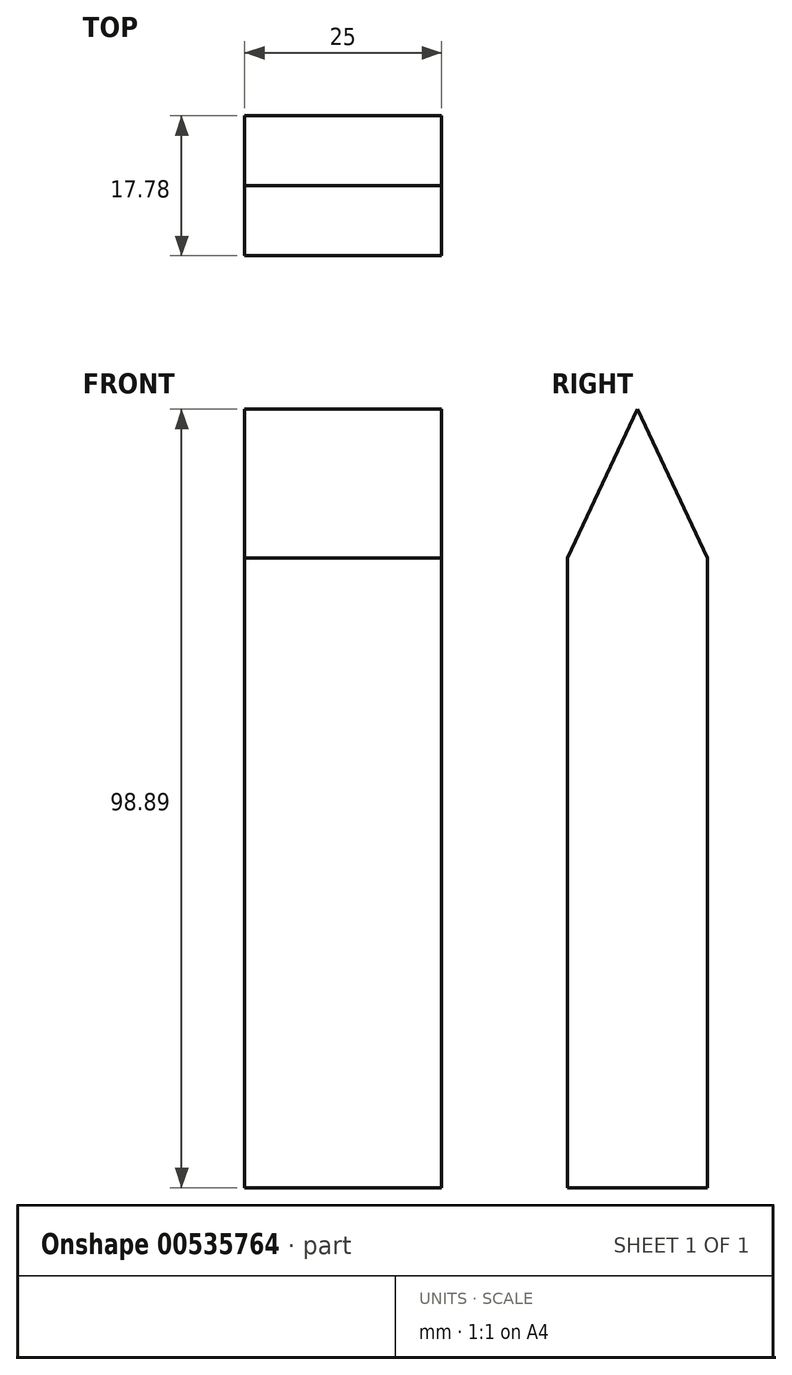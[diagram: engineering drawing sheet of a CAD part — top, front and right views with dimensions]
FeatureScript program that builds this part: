
annotation { "Feature Type Name" : "Feature", "Feature Type Description" : "" }
export const myFeature = defineFeature(function(context is Context, id is Id, definition is map)
    precondition{}
    {
        {
            var Q0;
            Q0=qCreatedBy(makeId("Right.planeOp"),FACE);
            var sketch = newSketch(context, id + "F0", { "sketchPlane" : qUnion([Q0])});
            skLineSegment(sketch, "E0", {"start": v(-35.56, 55.28) * mm, "end": v(-35.56, -24.72) * mm});
            skLineSegment(sketch, "E1", {"start": v(-35.56, -24.72) * mm, "end": v(-17.78, -24.72) * mm});
            skLineSegment(sketch, "E2", {"start": v(-17.78, -24.72) * mm, "end": v(-17.78, 55.28) * mm});
            skLineSegment(sketch, "E3", {"start": v(-17.78, 55.28) * mm, "end": v(-26.67, 74.17) * mm});
            skLineSegment(sketch, "E4", {"start": v(-26.67, 74.17) * mm, "end": v(-35.56, 55.28) * mm});
            skLineSegment(sketch, "E5", {"start": v(-62.22, 0) * mm, "end": v(-62.22, -22.5) * mm});
            skLineSegment(sketch, "E6", {"start": v(-62.22, 0) * mm, "end": v(-35.56, 15.28) * mm});
            skLineSegment(sketch, "E7", {"start": v(-62.22, -22.5) * mm, "end": v(-35.56, -8.06) * mm});
            skSolve(sketch);
        }
        {
            var Q0;
            {var subQ0=sQuery(id+"F0.wireOp",EDGE,"E1");Q0=makeQuery(id+"F0.imprint","IMPRINT",FACE,{"disambiguationData":[TD([[makeQuery(id+"F0.imprint","IMPRINT",EDGE,{"derivedFrom":subQ0}),1.0]])]});}
            extrude(context, id + "F1", {"entities" : qUnion([Q0]), "depth" : 25 * mm, "offsetDistance" : 25 * mm});
        }
    });
